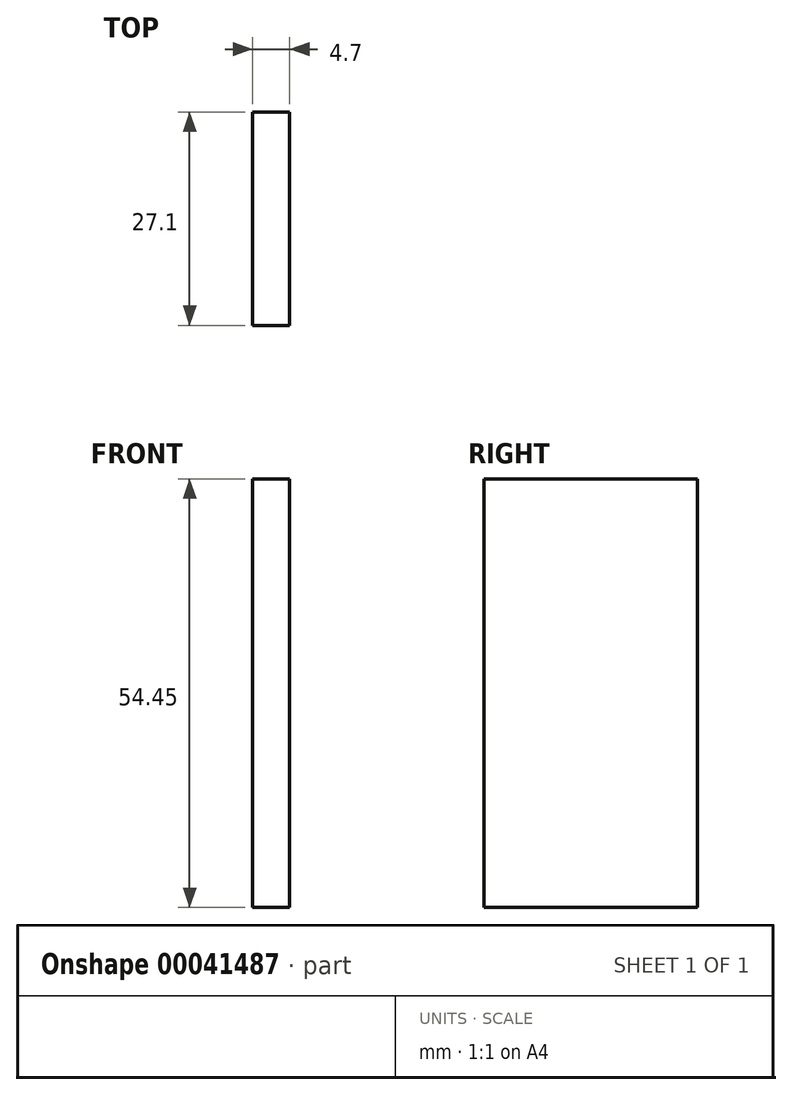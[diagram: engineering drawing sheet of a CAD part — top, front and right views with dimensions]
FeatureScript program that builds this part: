
annotation { "Feature Type Name" : "Feature", "Feature Type Description" : "" }
export const myFeature = defineFeature(function(context is Context, id is Id, definition is map)
    precondition{}
    {
        {
            var Q0;
            Q0=qCreatedBy(makeId("Front.planeOp"),FACE);
            var sketch = newSketch(context, id + "F0", { "sketchPlane" : qUnion([Q0])});
            skLineSegment(sketch, "E0.bottom", {"start": v(-2.15, 32.02) * mm, "end": v(2.55, 32.02) * mm});
            skLineSegment(sketch, "E0.top", {"start": v(-2.15, -22.43) * mm, "end": v(2.55, -22.43) * mm});
            skLineSegment(sketch, "E0.left", {"start": v(-2.15, 32.02) * mm, "end": v(-2.15, -22.43) * mm});
            skLineSegment(sketch, "E0.right", {"start": v(2.55, 32.02) * mm, "end": v(2.55, -22.43) * mm});
            skSolve(sketch);
        }
        {
            var Q0;
            Q0=makeQuery(id+"F0.imprint","IMPRINT",FACE,{"disambiguationData":[TD([[makeQuery(id+"F0.imprint","IMPRINT",EDGE,{"derivedFrom":sQuery(id+"F0.wireOp",EDGE,"E0.bottom")}),-1.0]])]});
            extrude(context, id + "F1", {"entities" : qUnion([Q0]), "depth" : 27.1 * mm});
        }
    });
